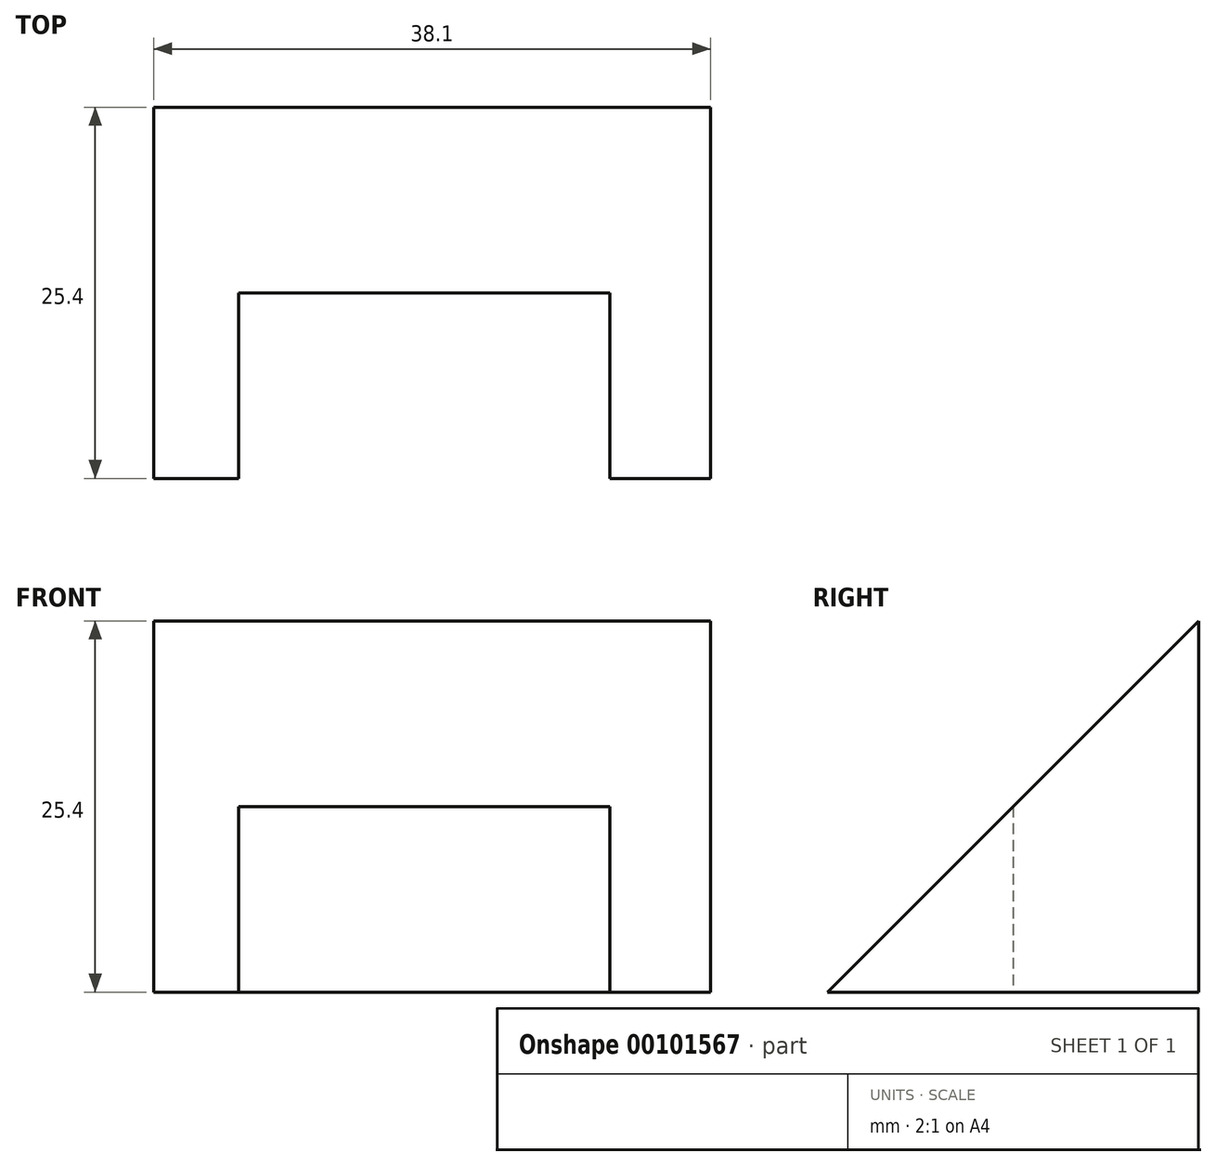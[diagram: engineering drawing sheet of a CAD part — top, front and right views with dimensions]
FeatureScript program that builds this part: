
annotation { "Feature Type Name" : "Feature", "Feature Type Description" : "" }
export const myFeature = defineFeature(function(context is Context, id is Id, definition is map)
    precondition{}
    {
        {
            var Q0;
            Q0=qCreatedBy(makeId("Right.planeOp"),FACE);
            var sketch = newSketch(context, id + "F0", { "sketchPlane" : qUnion([Q0])});
            skLineSegment(sketch, "E0", {"start": v(0, 0) * mm, "end": v(0, 25.4) * mm});
            skLineSegment(sketch, "E1", {"start": v(0, 25.4) * mm, "end": v(-25.4, 0) * mm});
            skLineSegment(sketch, "E2", {"start": v(-25.4, 0) * mm, "end": v(0, 0) * mm});
            skSolve(sketch);
        }
        {
            var Q0;
            Q0 = qSketchRegion(id + "F0", true);
            extrude(context, id + "F1", {"entities" : qUnion([Q0]), "endBound" : BoundingType.SYMMETRIC, "oppositeDirection" : true, "depth" : 38.1 * mm});
        }
        {
            var Q0;
            Q0=qCreatedBy(makeId("Top.planeOp"),FACE);
            var sketch = newSketch(context, id + "F2", { "sketchPlane" : qUnion([Q0])});
            skLineSegment(sketch, "E3", {"start": v(-13.23, -25.4) * mm, "end": v(12.17, -25.4) * mm});
            skLineSegment(sketch, "E4", {"start": v(12.17, -25.4) * mm, "end": v(12.17, -12.7) * mm});
            skLineSegment(sketch, "E5", {"start": v(12.17, -12.7) * mm, "end": v(-13.23, -12.7) * mm});
            skLineSegment(sketch, "E6", {"start": v(-13.23, -12.7) * mm, "end": v(-13.23, -25.4) * mm});
            skSolve(sketch);
        }
        {
            var Q0;
            Q0 = qSketchRegion(id + "F2", true);
            extrude(context, id + "F3", {"entities" : qUnion([Q0]), "operationType" : NewBodyOperationType.REMOVE, "endBound" : BoundingType.THROUGH_ALL, "depth" : 25.4 * mm});
        }
    });
